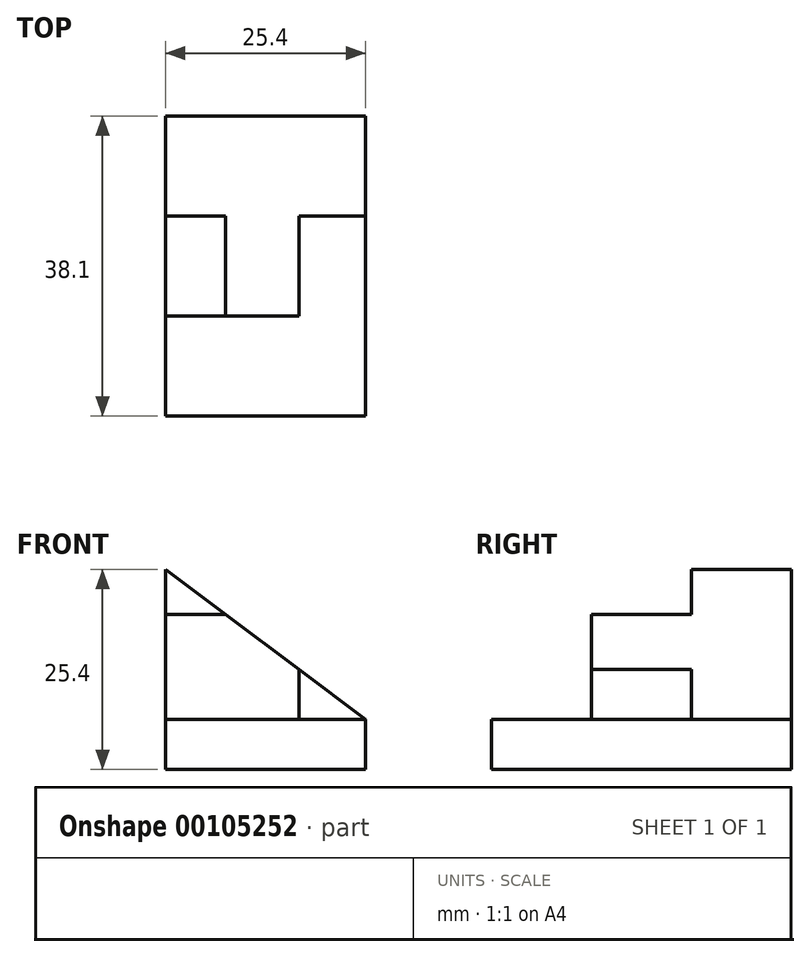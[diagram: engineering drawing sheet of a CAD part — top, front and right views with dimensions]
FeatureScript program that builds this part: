
annotation { "Feature Type Name" : "Feature", "Feature Type Description" : "" }
export const myFeature = defineFeature(function(context is Context, id is Id, definition is map)
    precondition{}
    {
        {
            var Q0;
            Q0=qCreatedBy(makeId("Front.planeOp"),FACE);
            var sketch = newSketch(context, id + "F0", { "sketchPlane" : qUnion([Q0])});
            skLineSegment(sketch, "E0.bottom", {"start": v(0, 0) * mm, "end": v(25.4, 0) * mm});
            skLineSegment(sketch, "E0.top", {"start": v(0, 6.35) * mm, "end": v(25.4, 6.35) * mm});
            skLineSegment(sketch, "E0.left", {"start": v(0, 0) * mm, "end": v(0, 6.35) * mm});
            skLineSegment(sketch, "E0.right", {"start": v(25.4, 0) * mm, "end": v(25.4, 6.35) * mm});
            skSolve(sketch);
        }
        {
            var Q0;
            Q0 = qSketchRegion(id + "F0", true);
            extrude(context, id + "F1", {"entities" : qUnion([Q0]), "depth" : 38.1 * mm});
        }
        {
            var Q0;
            Q0=qCreatedBy(makeId("Front.planeOp"),FACE);
            var sketch = newSketch(context, id + "F2", { "sketchPlane" : qUnion([Q0])});
            skLineSegment(sketch, "E1", {"start": v(0, 6.35) * mm, "end": v(0, 25.4) * mm});
            skLineSegment(sketch, "E2", {"start": v(0, 25.4) * mm, "end": v(25.4, 6.35) * mm});
            skLineSegment(sketch, "E3", {"start": v(25.4, 6.35) * mm, "end": v(0, 6.35) * mm});
            skSolve(sketch);
        }
        {
            var Q0;
            Q0 = qSketchRegion(id + "F2", true);
            extrude(context, id + "F3", {"entities" : qUnion([Q0]), "operationType" : NewBodyOperationType.ADD, "depth" : 12.7 * mm});
        }
        {
            var Q0;
            Q0=makeQuery(id+"F3.opExtrude","CAP_FACE",FACE,{"disambiguationData":[OSD([sQuery(id+"F2.wireOp",EDGE,"E1"),sQuery(id+"F2.wireOp",EDGE,"E2"),sQuery(id+"F2.wireOp",EDGE,"E3")])],"isStart":false});
            var sketch = newSketch(context, id + "F4", { "sketchPlane" : qUnion([Q0])});
            skLineSegment(sketch, "E4", {"start": v(0, 6.35) * mm, "end": v(0, 19.68) * mm});
            skLineSegment(sketch, "E5", {"start": v(0, 19.68) * mm, "end": v(7.62, 19.68) * mm});
            skLineSegment(sketch, "E6", {"start": v(7.62, 19.69) * mm, "end": v(16.93, 12.7) * mm});
            skLineSegment(sketch, "E7", {"start": v(16.93, 12.7) * mm, "end": v(16.93, 6.35) * mm});
            skLineSegment(sketch, "E8", {"start": v(16.93, 6.35) * mm, "end": v(0, 6.35) * mm});
            skSolve(sketch);
        }
        {
            var Q0;
            Q0 = qSketchRegion(id + "F4", true);
            extrude(context, id + "F5", {"entities" : qUnion([Q0]), "operationType" : NewBodyOperationType.ADD, "depth" : 12.7 * mm});
        }
    });
